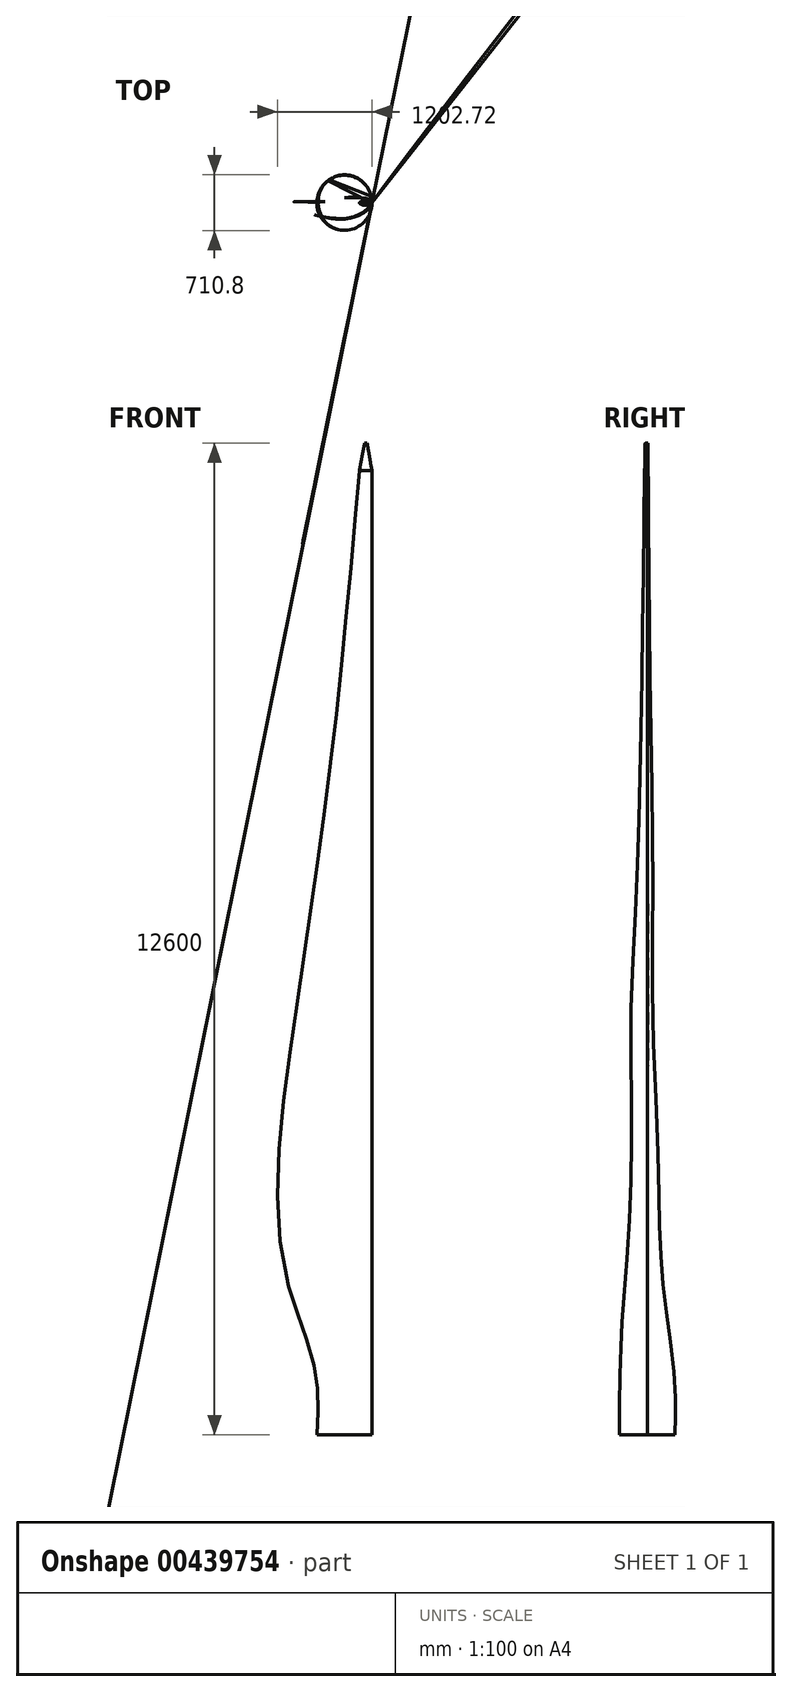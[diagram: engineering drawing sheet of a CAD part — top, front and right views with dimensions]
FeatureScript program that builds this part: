
annotation { "Feature Type Name" : "Feature", "Feature Type Description" : "" }
export const myFeature = defineFeature(function(context is Context, id is Id, definition is map)
    precondition{}
    {
        {
            var Q0;
            Q0=qCreatedBy(makeId("Top.planeOp"),FACE);
            var sketch = newSketch(context, id + "F0", { "sketchPlane" : qUnion([Q0])});
            skCircle(sketch, "E0", {"center": v(0, 0) * mm, "radius": 1000 * mm});
            skLineSegment(sketch, "E1.bottom", {"start": v(851.1, 525) * mm, "end": v(-851.1, 525) * mm, "construction": true});
            skLineSegment(sketch, "E1.top", {"start": v(851.1, -525) * mm, "end": v(-851.1, -525) * mm, "construction": true});
            skLineSegment(sketch, "E1.left", {"start": v(851.1, 525) * mm, "end": v(851.1, -525) * mm, "construction": true});
            skLineSegment(sketch, "E1.right", {"start": v(-851.1, 525) * mm, "end": v(-851.1, -525) * mm, "construction": true});
            skLineSegment(sketch, "E2", {"start": v(851.1, 0) * mm, "end": v(0, 0) * mm, "construction": true});
            skSolve(sketch);
        }
        {
            var Q0;
            Q0=qCreatedBy(makeId("Top.planeOp"),FACE);
            cPlane(context, id + "F1", {"entities" : qUnion([Q0]), "cplaneType" : CPlaneType.OFFSET, "offset" : 2000 * mm, "width" : 150 * mm, "height" : 150 * mm});
        }
        {
            var Q0;
            Q0=qCreatedBy(id+"F1.planeOp",FACE);
            var sketch = newSketch(context, id + "F2", { "sketchPlane" : qUnion([Q0])});
            skCircle(sketch, "E3.0", {"center": v(0, 0) * mm, "radius": 1000 * mm});
            skLineSegment(sketch, "E3.1", {"start": v(851.1, 525) * mm, "end": v(-851.1, 525) * mm, "construction": true});
            skLineSegment(sketch, "E3.2", {"start": v(851.1, -525) * mm, "end": v(-851.1, -525) * mm, "construction": true});
            skLineSegment(sketch, "E3.3", {"start": v(851.1, 525) * mm, "end": v(851.1, -525) * mm, "construction": true});
            skLineSegment(sketch, "E3.4", {"start": v(-851.1, 525) * mm, "end": v(-851.1, -525) * mm, "construction": true});
            skLineSegment(sketch, "E3.5", {"start": v(851.1, 0) * mm, "end": v(0, 0) * mm, "construction": true});
            skSolve(sketch);
        }
        {
            var Q0;
            Q0=qCreatedBy(id+"F1.planeOp",FACE);
            cPlane(context, id + "F3", {"entities" : qUnion([Q0]), "cplaneType" : CPlaneType.OFFSET, "offset" : 3000 * mm, "width" : 150 * mm, "height" : 150 * mm});
        }
        {
            var Q0;
            Q0=qCreatedBy(id+"F3.planeOp",FACE);
            var sketch = newSketch(context, id + "F4", { "sketchPlane" : qUnion([Q0])});
            skCircle(sketch, "E4.0", {"center": v(0, 0) * mm, "radius": 1000 * mm, "construction": true});
            skLineSegment(sketch, "E5", {"start": v(1000, 0) * mm, "end": v(-1905.76, 0) * mm, "construction": true});
            skArc(sketch, "E6", {"start": v(-1905.76, 0) * mm, "mid": v(-452.88, -86.82) * mm, "end": v(1000, 0) * mm, "construction": true});
            skCircle(sketch, "E7", {"center": v(-260.37, -85.3) * mm, "radius": 806.72 * mm, "construction": true});
            skFitSpline(sketch, "E8", {"points": [v(-1905.76, 0) * mm, v(-538.74, -842.47) * mm, v(895.67, -232.44) * mm, v(1000, 0) * mm, v(895.78, 292.95) * mm, v(-681.52, 602.75) * mm, v(-1401.57, 263.18) * mm, v(-1905.76, 0) * mm]});
            skSolve(sketch);
        }
        {
            var Q0;
            Q0=qCreatedBy(id+"F3.planeOp",FACE);
            cPlane(context, id + "F5", {"entities" : qUnion([Q0]), "cplaneType" : CPlaneType.OFFSET, "offset" : 5000 * mm, "width" : 150 * mm, "height" : 150 * mm});
        }
        {
            var Q0;
            Q0=qCreatedBy(id+"F5.planeOp",FACE);
            var sketch = newSketch(context, id + "F6", { "sketchPlane" : qUnion([Q0])});
            skLineSegment(sketch, "E9.1", {"start": v(1000, 0) * mm, "end": v(-1905.76, 0) * mm, "construction": true});
            skCircle(sketch, "E9.3", {"center": v(-393.94, -162.13) * mm, "radius": 564.66 * mm, "construction": true});
            skArc(sketch, "E10", {"start": v(-2392.9, 0) * mm, "mid": v(-696.45, -167.4) * mm, "end": v(1000, 0) * mm, "construction": true});
            skLineSegment(sketch, "E11", {"start": v(1000, 0) * mm, "end": v(-2392.9, 0) * mm, "construction": true});
            skFitSpline(sketch, "E12", {"points": [v(-2392.9, 0) * mm, v(0, -566.66) * mm, v(955.1, -116.34) * mm, v(1000, 0) * mm, v(938.88, 167.52) * mm, v(-274.25, 389.69) * mm, v(-1746.7, 78.8) * mm, v(-2392.9, 0) * mm]});
            skSolve(sketch);
        }
        {
            var Q0;
            Q0=qCreatedBy(id+"F5.planeOp",FACE);
            cPlane(context, id + "F7", {"entities" : qUnion([Q0]), "cplaneType" : CPlaneType.OFFSET, "offset" : 5000 * mm, "width" : 150 * mm, "height" : 150 * mm});
        }
        {
            var Q0;
            Q0=qCreatedBy(id+"F7.planeOp",FACE);
            var sketch = newSketch(context, id + "F8", { "sketchPlane" : qUnion([Q0])});
            skLineSegment(sketch, "E13.0", {"start": v(1000, 0) * mm, "end": v(-1905.76, 0) * mm, "construction": true});
            skCircle(sketch, "E13.1", {"center": v(-41.55, -197.63) * mm, "radius": 399.22 * mm, "construction": true});
            skLineSegment(sketch, "E13.3", {"start": v(1000, 0) * mm, "end": v(-2392.9, 0) * mm, "construction": true});
            skFitSpline(sketch, "E13.4", {"points": [v(-2392.9, 0) * mm, v(-2338.2, -131.99) * mm, v(109.83, -949.56) * mm, v(962.16, -156.54) * mm, v(1007.07, -4.51) * mm, v(991.32, 275.8) * mm, v(-412.14, 543.94) * mm, v(-1541.72, -2.41) * mm, v(-2421.05, 67.91) * mm, v(-2392.9, 0) * mm], "construction": true});
            skArc(sketch, "E14", {"start": v(-1816.62, 0) * mm, "mid": v(-408.31, -211.69) * mm, "end": v(1000, 0) * mm, "construction": true});
            skFitSpline(sketch, "E15", {"points": [v(-1816.62, 0) * mm, v(-75.33, -595.41) * mm, v(945.5, -129.55) * mm, v(1000, 0) * mm, v(933.83, 97.72) * mm, v(-75.33, 200.16) * mm, v(-1151.9, 32.5) * mm, v(-1816.62, 0) * mm]});
            skSolve(sketch);
        }
        {
            var Q0;
            Q0=qCreatedBy(id+"F7.planeOp",FACE);
            cPlane(context, id + "F9", {"entities" : qUnion([Q0]), "cplaneType" : CPlaneType.OFFSET, "offset" : 5000 * mm, "width" : 150 * mm, "height" : 150 * mm});
        }
        {
            var Q0;
            Q0=qCreatedBy(id+"F9.planeOp",FACE);
            var sketch = newSketch(context, id + "F10", { "sketchPlane" : qUnion([Q0])});
            skLineSegment(sketch, "E16.0", {"start": v(1000, 0) * mm, "end": v(-1905.76, 0) * mm, "construction": true});
            skCircle(sketch, "E16.1", {"center": v(75.87, -95.47) * mm, "radius": 277.22 * mm, "construction": true});
            skLineSegment(sketch, "E16.2", {"start": v(1000, 0) * mm, "end": v(-2392.9, 0) * mm, "construction": true});
            skArc(sketch, "E17", {"start": v(-1078.3, 0) * mm, "mid": v(-39.15, -96.65) * mm, "end": v(1000, 0) * mm, "construction": true});
            skFitSpline(sketch, "E18", {"points": [v(-1078.3, 0) * mm, v(30.74, -369) * mm, v(915.63, -167.35) * mm, v(1000, 0) * mm, v(872.32, 136.27) * mm, v(30.74, 178.05) * mm, v(-533.72, 47.05) * mm, v(-1078.3, 0) * mm]});
            skSolve(sketch);
        }
        {
            var Q0;
            Q0=qCreatedBy(id+"F9.planeOp",FACE);
            cPlane(context, id + "F11", {"entities" : qUnion([Q0]), "cplaneType" : CPlaneType.OFFSET, "offset" : 15000 * mm, "width" : 150 * mm, "height" : 150 * mm});
        }
        {
            var Q0;
            Q0=qCreatedBy(id+"F11.planeOp",FACE);
            var sketch = newSketch(context, id + "F12", { "sketchPlane" : qUnion([Q0])});
            skLineSegment(sketch, "E19.0", {"start": v(1000, 0) * mm, "end": v(-1905.76, 0) * mm, "construction": true});
            skLineSegment(sketch, "E19.2", {"start": v(1000, 0) * mm, "end": v(-2392.9, 0) * mm, "construction": true});
            skCircle(sketch, "E20", {"center": v(780.88, -29.93) * mm, "radius": 74.07 * mm, "construction": true});
            skArc(sketch, "E21", {"start": v(540.83, 0) * mm, "mid": v(770.42, -29.99) * mm, "end": v(1000, 0) * mm, "construction": true});
            skFitSpline(sketch, "E22", {"points": [v(540.83, 0) * mm, v(738.5, -90.67) * mm, v(985.23, -35.23) * mm, v(1000, 0) * mm, v(979.68, 25.85) * mm, v(734.03, 27.44) * mm, v(574.3, 31.4) * mm, v(540.83, 0) * mm]});
            skSolve(sketch);
        }
        {
            var Q0;
            Q0=qCreatedBy(id+"F11.planeOp",FACE);
            cPlane(context, id + "F13", {"entities" : qUnion([Q0]), "cplaneType" : CPlaneType.OFFSET, "offset" : 1000 * mm, "oppositeDirection" : true, "width" : 150 * mm, "height" : 150 * mm});
        }
        {
            var Q0;
            Q0=qCreatedBy(id+"F9.planeOp",FACE);
            cPlane(context, id + "F14", {"entities" : qUnion([Q0]), "cplaneType" : CPlaneType.OFFSET, "offset" : 5000 * mm, "width" : 150 * mm, "height" : 150 * mm});
        }
        {
            var Q0;
            Q0=qCreatedBy(id+"F14.planeOp",FACE);
            var sketch = newSketch(context, id + "F15", { "sketchPlane" : qUnion([Q0])});
            skLineSegment(sketch, "E23.0", {"start": v(1000, 0) * mm, "end": v(-1905.76, 0) * mm, "construction": true});
            skCircle(sketch, "E23.1", {"center": v(462.37, -47.75) * mm, "radius": 187.93 * mm, "construction": true});
            skArc(sketch, "E24", {"start": v(-426.95, 0) * mm, "mid": v(286.52, -50.82) * mm, "end": v(1000, 0) * mm, "construction": true});
            skFitSpline(sketch, "E25", {"points": [v(-426.95, 0) * mm, v(444.7, -234.84) * mm, v(977.35, -48.24) * mm, v(1000, 0) * mm, v(966.35, 61.82) * mm, v(464.87, 140.17) * mm, v(-44.05, 48.62) * mm, v(-426.95, 0) * mm]});
            skSolve(sketch);
        }
        {
            var Q0;
            Q0=qCreatedBy(id+"F11.planeOp",FACE);
            cPlane(context, id + "F16", {"entities" : qUnion([Q0]), "cplaneType" : CPlaneType.OFFSET, "offset" : 1000 * mm, "width" : 150 * mm, "height" : 150 * mm});
        }
        {
            var Q0;
            Q0=qCreatedBy(id+"F16.planeOp",FACE);
            var sketch = newSketch(context, id + "F17", { "sketchPlane" : qUnion([Q0])});
            skCircle(sketch, "E26", {"center": v(781.13, -27.33) * mm, "radius": 46.13 * mm});
            skSolve(sketch);
        }
        {
            var Q0;
            Q0=qCreatedBy(id+"F16.planeOp",FACE);
            cPlane(context, id + "F18", {"entities" : qUnion([Q0]), "cplaneType" : CPlaneType.OFFSET, "offset" : 1000 * mm, "width" : 150 * mm, "height" : 150 * mm});
        }
        {
            var Q0;
            Q0=makeQuery(id+"F0.imprint","IMPRINT",FACE,{"disambiguationData":[TD([[makeQuery(id+"F0.imprint","IMPRINT",EDGE,{"derivedFrom":sQuery(id+"F0.wireOp",EDGE,"E0")}),1.0]])]});
            var Q1;
            Q1=makeQuery(id+"F2.imprint","IMPRINT",FACE,{"disambiguationData":[TD([[makeQuery(id+"F2.imprint","IMPRINT",EDGE,{"derivedFrom":sQuery(id+"F2.wireOp",EDGE,"E3.0")}),1.0]])]});
            var Q2;
            Q2=makeQuery(id+"F4.imprint","IMPRINT",FACE,{"disambiguationData":[TD([[makeQuery(id+"F4.imprint","IMPRINT",EDGE,{"derivedFrom":sQuery(id+"F4.wireOp",EDGE,"E8")}),1.0]])]});
            var Q3;
            Q3=makeQuery(id+"F6.imprint","IMPRINT",FACE,{"disambiguationData":[TD([[makeQuery(id+"F6.imprint","IMPRINT",EDGE,{"derivedFrom":sQuery(id+"F6.wireOp",EDGE,"E12")}),1.0]])]});
            var Q4;
            Q4=makeQuery(id+"F8.imprint","IMPRINT",FACE,{"disambiguationData":[TD([[makeQuery(id+"F8.imprint","IMPRINT",EDGE,{"derivedFrom":sQuery(id+"F8.wireOp",EDGE,"E15")}),1.0]])]});
            var Q5;
            Q5=makeQuery(id+"F10.imprint","IMPRINT",FACE,{"disambiguationData":[TD([[makeQuery(id+"F10.imprint","IMPRINT",EDGE,{"derivedFrom":sQuery(id+"F10.wireOp",EDGE,"E18")}),1.0]])]});
            var Q6;
            Q6=makeQuery(id+"F15.imprint","IMPRINT",FACE,{"disambiguationData":[TD([[makeQuery(id+"F15.imprint","IMPRINT",EDGE,{"derivedFrom":sQuery(id+"F15.wireOp",EDGE,"E25")}),1.0]])]});
            var Q7;
            Q7=makeQuery(id+"F12.imprint","IMPRINT",FACE,{"disambiguationData":[TD([[makeQuery(id+"F12.imprint","IMPRINT",EDGE,{"derivedFrom":sQuery(id+"F12.wireOp",EDGE,"E22")}),1.0]])]});
            loft(context, id + "F19", {"sheetProfilesArray" : [{ "sheetProfileEntities" : qUnion([Q0]) }, { "sheetProfileEntities" : qUnion([Q1]) }, { "sheetProfileEntities" : qUnion([Q2]) }, { "sheetProfileEntities" : qUnion([Q3]) }, { "sheetProfileEntities" : qUnion([Q4]) }, { "sheetProfileEntities" : qUnion([Q5]) }, { "sheetProfileEntities" : qUnion([Q6]) }, { "sheetProfileEntities" : qUnion([Q7]) }]});
        }
        {
            var Q0;
            Q0=makeQuery(id+"F12.imprint","IMPRINT",FACE,{"disambiguationData":[TD([[makeQuery(id+"F12.imprint","IMPRINT",EDGE,{"derivedFrom":sQuery(id+"F12.wireOp",EDGE,"E22")}),1.0]])]});
            var Q1;
            Q1=makeQuery(id+"F17.imprint","IMPRINT",FACE,{"disambiguationData":[TD([[makeQuery(id+"F17.imprint","IMPRINT",EDGE,{"derivedFrom":sQuery(id+"F17.wireOp",EDGE,"E26")}),1.0]])]});
            loft(context, id + "F20", {"operationType" : NewBodyOperationType.ADD, "sheetProfilesArray" : [{ "sheetProfileEntities" : qUnion([Q0]) }, { "sheetProfileEntities" : qUnion([Q1]) }]});
        }
        {
            var Q0;
            Q0=makeQuery(id+"F19.opLoft","SWEPT_BODY",BODY,{"disambiguationData":[OSD([makeQuery(id+"F0.imprint","IMPRINT",FACE,{"disambiguationData":[TD([[makeQuery(id+"F0.imprint","IMPRINT",EDGE,{"derivedFrom":sQuery(id+"F0.wireOp",EDGE,"E0")}),1.0]])]}),sQuery(id+"F2.wireOp",EDGE,"E3.0"),sQuery(id+"F4.wireOp",EDGE,"E8"),sQuery(id+"F6.wireOp",EDGE,"E12"),sQuery(id+"F8.wireOp",EDGE,"E15"),sQuery(id+"F10.wireOp",EDGE,"E18"),makeQuery(id+"F12.imprint","IMPRINT",FACE,{"disambiguationData":[TD([[makeQuery(id+"F12.imprint","IMPRINT",EDGE,{"derivedFrom":sQuery(id+"F12.wireOp",EDGE,"E22")}),1.0]])]}),sQuery(id+"F15.wireOp",EDGE,"E25")])]});
            var Q1;
            Q1=qCreatedBy(makeId("Origin.pointOp"),VERTEX);
            transform(context, id + "F21", {"entities" : qUnion([Q0]), "transformType" : TransformType.SCALE_UNIFORMLY, "scale" : .35, "scalePoint" : qUnion([Q1]), "makeCopy" : false});
        }
    });
